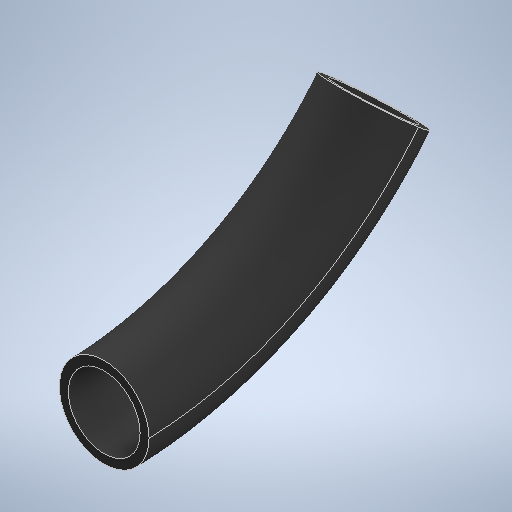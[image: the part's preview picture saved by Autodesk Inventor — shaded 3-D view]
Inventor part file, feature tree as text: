
AUTODESK INVENTOR PART (.ipt)
format: ipt  version: 2025.2 (Build 292293000, 293)  size: 315,904 bytes
history: native  units: mm
features: sketch x2, other x1, sweep x1
ambient origin geometry x8: Origin, YZ Plane, XZ Plane, XY Plane, X Axis, Y Axis, Z Axis, Center Point
bodies: Body1 (feature_tree)
feature tree (4):
  other  "Sólido1"
  sweep  "Varredura1"
  sketch  "Esboço1"  dims[d0=10.0mm d1=1.0mm]
  sketch  "Esboço2"  dims[d5=40.0mm d6=15.0mm d7=30.0mm d8=0.0mm d9=0.0mm]
